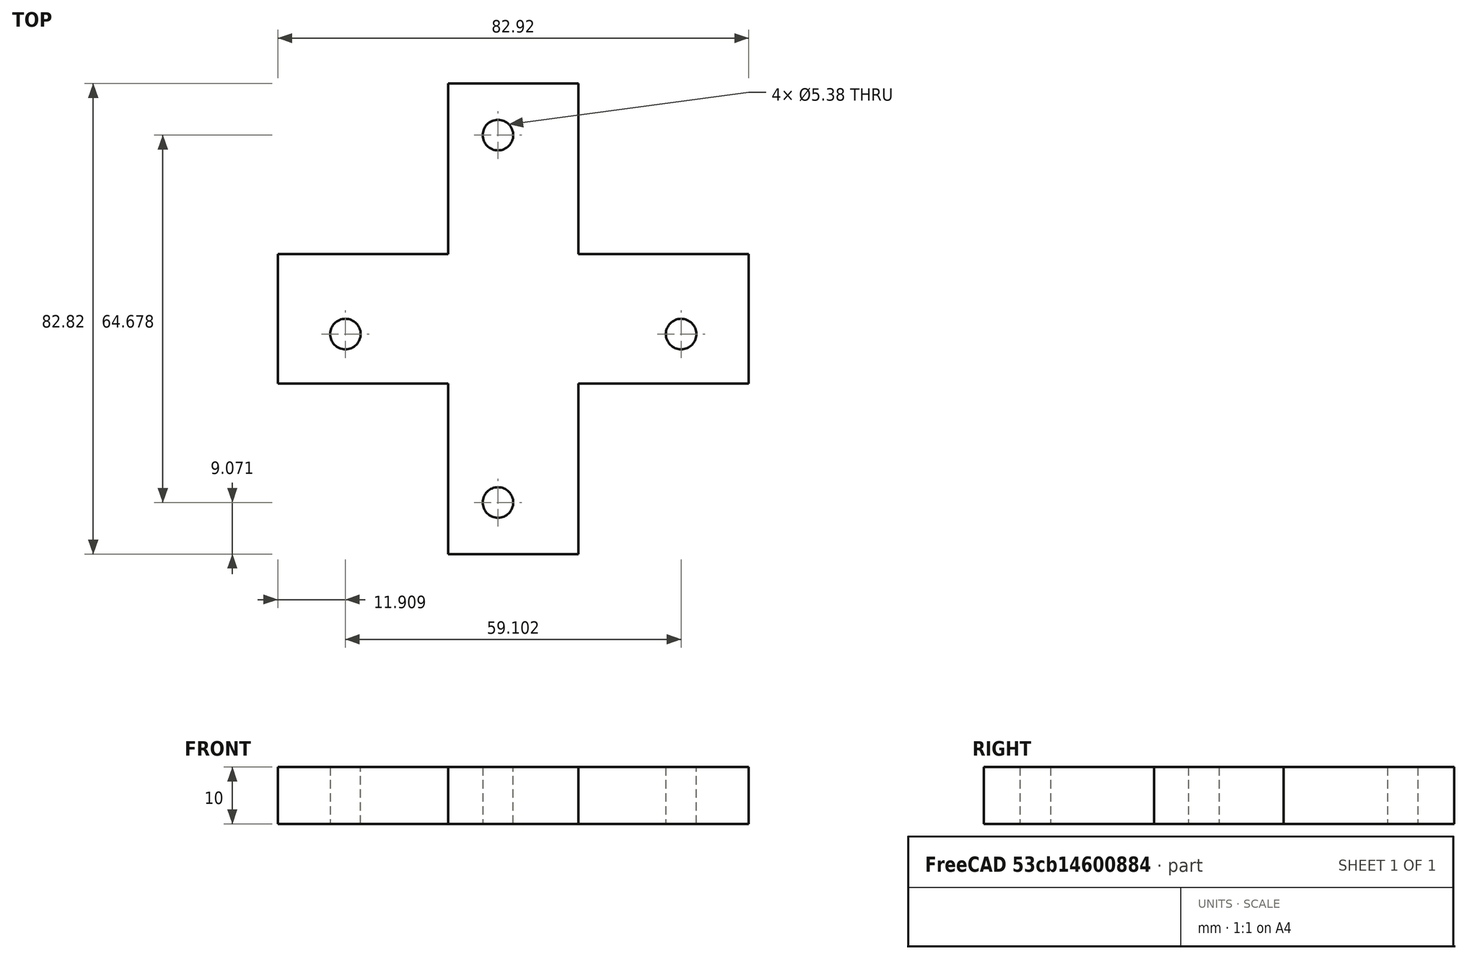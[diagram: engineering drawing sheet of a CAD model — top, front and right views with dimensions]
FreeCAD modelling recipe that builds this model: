
FCSTD DOCUMENT  (FreeCAD 0.21R33694 (Git))
Label: OJT1_T19R02_creu
License: All rights reserved
LicenseURL: https://en.wikipedia.org/wiki/All_rights_reserved
objects: Sketcher::SketchObject×1, PartDesign::Pad×1, PartDesign::Body×1
note: 4 computed .brp shape members not serialized (recipe doc carries the construction recipe); baked Part::Feature solids carry a one-line shape summary decoded from their .brp

FEATURE [Sketcher::SketchObject] Sketch
  FullyConstrained = false
  MapMode = 5
  Support = -> [XY_Plane]
  sketch-geometry (16):
    g0: LineSegment StartX=11.4604 StartY=11.4063 StartZ=0 EndX=11.4604 EndY=41.4063 EndZ=0
    g1: LineSegment StartX=11.4604 StartY=41.4063 StartZ=0 EndX=-11.4604 EndY=41.4063 EndZ=0
    g2: LineSegment StartX=-11.4604 StartY=41.4063 StartZ=0 EndX=-11.4604 EndY=11.4063 EndZ=0
    g3: LineSegment StartX=-11.4604 StartY=11.4063 StartZ=0 EndX=-41.4604 EndY=11.4063 EndZ=0
    g4: LineSegment StartX=-41.4604 StartY=11.4063 StartZ=0 EndX=-41.4604 EndY=-11.4063 EndZ=0
    g5: LineSegment StartX=-41.4604 StartY=-11.4063 StartZ=0 EndX=-11.4604 EndY=-11.4063 EndZ=0
    g6: LineSegment StartX=-11.4604 StartY=-11.4063 StartZ=0 EndX=-11.4604 EndY=-41.4063 EndZ=0
    g7: LineSegment StartX=-11.4604 StartY=-41.4063 StartZ=0 EndX=11.4604 EndY=-41.4063 EndZ=0
    g8: LineSegment StartX=11.4604 StartY=-41.4063 StartZ=0 EndX=11.4604 EndY=-11.4063 EndZ=0
    g9: LineSegment StartX=11.4604 StartY=-11.4063 StartZ=0 EndX=41.4604 EndY=-11.4063 EndZ=0
    g10: LineSegment StartX=41.4604 StartY=-11.4063 StartZ=0 EndX=41.4604 EndY=11.4063 EndZ=0
    g11: LineSegment StartX=41.4604 StartY=11.4063 StartZ=0 EndX=11.4604 EndY=11.4063 EndZ=0
    g12: Circle CenterX=29.5509 CenterY=-2.69065 CenterZ=0 NormalX=0 NormalY=0 NormalZ=1 AngleXU=0 Radius=2.69065
    g13: Circle CenterX=-2.69065 CenterY=-32.3389 CenterZ=0 NormalX=0 NormalY=0 NormalZ=1 AngleXU=0 Radius=2.69065
    g14: Circle CenterX=-29.5509 CenterY=-2.69065 CenterZ=0 NormalX=0 NormalY=0 NormalZ=1 AngleXU=0 Radius=2.69065
    g15: Circle CenterX=-2.69065 CenterY=32.3389 CenterZ=0 NormalX=0 NormalY=0 NormalZ=1 AngleXU=0 Radius=2.69065
  constraints (39):
    c: Vertical(g0)
    c: Coincident(g0,g1)
    c: Horizontal(g1)
    c: Coincident(g1,g2)
    c: Vertical(g2)
    c: Coincident(g2,g3)
    c: Horizontal(g3)
    c: Coincident(g3,g4)
    c: Vertical(g4)
    c: Coincident(g4,g5)
    c: Horizontal(g5)
    c: Coincident(g5,g6)
    c: Vertical(g6)
    c: Coincident(g6,g7)
    c: Horizontal(g7)
    c: Coincident(g7,g8)
    c: Vertical(g8)
    c: Coincident(g8,g9)
    c: Horizontal(g9)
    c: Coincident(g9,g10)
    c: Vertical(g10)
    c: Coincident(g10,g11)
    c: Coincident(g11,g0)
    c: Equal(g5,g9)
    c: DistanceX(g5,g5) = 30
    c: Equal(g3,g11)
    c: Equal(g2,g6)
    c: DistanceY(g2,g2) = 30
    c: Equal(g4,g10)
    c: Symmetric(g2,g0,g-2)
    c: Symmetric(g2,g5,g-1)
    c: Tangent(g13,g-2)
    c: Tangent(g14,g-1)
    c: Equal(g14,g12)
    c: Equal(g12,g13)
    c: Equal(g13,g15)
    c: Symmetric(g14,g12,g-2)
    c: Symmetric(g15,g13,g-1)
    c: Symmetric(g5,g8,g-2)
FEATURE [PartDesign::Pad] Pad
  Direction = (0,0,1)
  Length = 10
  Length2 = 10
  Profile = -> Sketch
  ReferenceAxis = -> Sketch [N_Axis]
  Type = 0
FEATURE [PartDesign::Body] Body
  Group = -> [Sketch,Pad]
  Origin = -> Origin
  Tip = -> Pad
